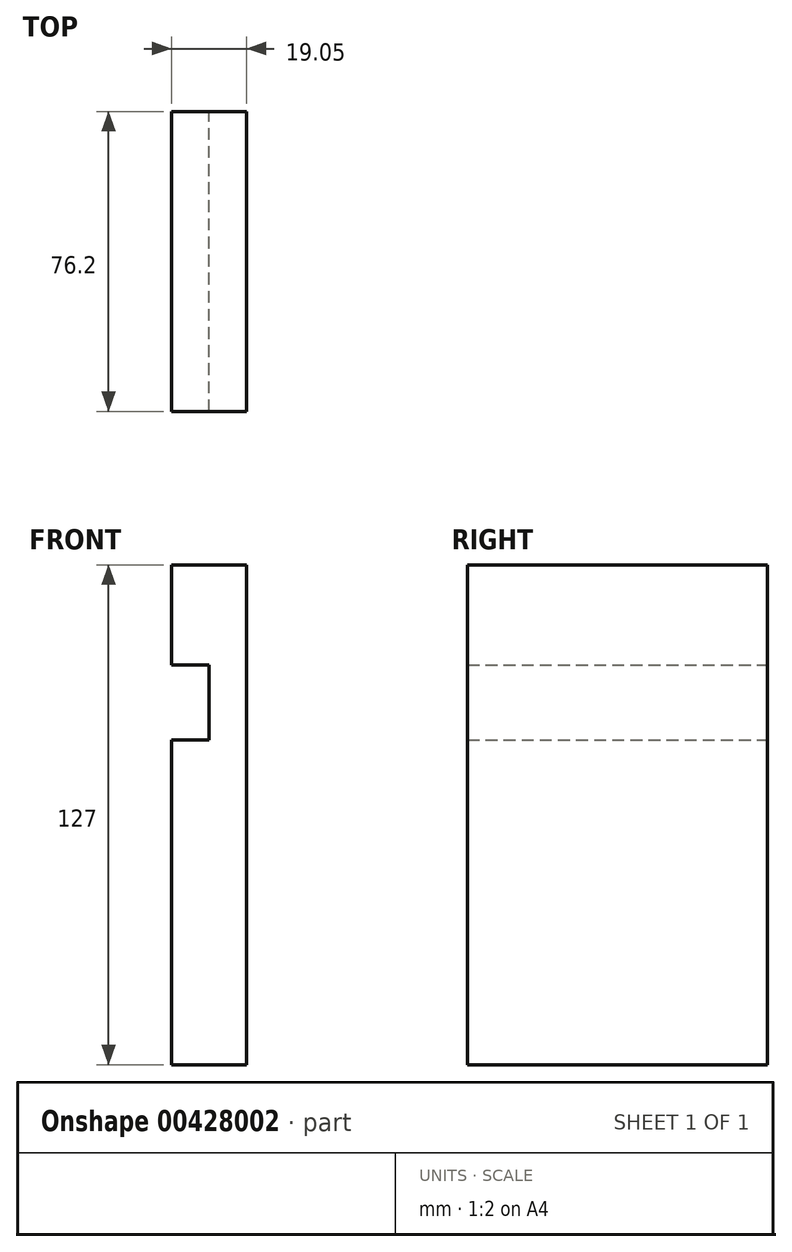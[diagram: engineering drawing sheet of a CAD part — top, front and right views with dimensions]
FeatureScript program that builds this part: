
annotation { "Feature Type Name" : "Feature", "Feature Type Description" : "" }
export const myFeature = defineFeature(function(context is Context, id is Id, definition is map)
    precondition{}
    {
        {
            var Q0;
            Q0=qCreatedBy(makeId("Front.planeOp"),FACE);
            var sketch = newSketch(context, id + "F0", { "sketchPlane" : qUnion([Q0])});
            skLineSegment(sketch, "E0", {"start": v(0, 0) * mm, "end": v(0, 127) * mm});
            skLineSegment(sketch, "E1", {"start": v(0, 0) * mm, "end": v(-19.05, 0) * mm});
            skLineSegment(sketch, "E2", {"start": v(0, 127) * mm, "end": v(-19.05, 127) * mm});
            skLineSegment(sketch, "E3", {"start": v(-19.05, 127) * mm, "end": v(-19.05, 101.6) * mm});
            skLineSegment(sketch, "E4", {"start": v(-19.05, 101.6) * mm, "end": v(-9.53, 101.6) * mm});
            skLineSegment(sketch, "E5", {"start": v(-9.53, 101.6) * mm, "end": v(-9.53, 82.55) * mm});
            skLineSegment(sketch, "E6", {"start": v(-9.53, 82.55) * mm, "end": v(-19.05, 82.55) * mm});
            skLineSegment(sketch, "E7", {"start": v(-19.05, 82.55) * mm, "end": v(-19.05, 0) * mm});
            skSolve(sketch);
        }
        {
            var Q0;
            Q0 = qSketchRegion(id + "F0", true);
            extrude(context, id + "F1", {"entities" : qUnion([Q0]), "depth" : 76.2 * mm});
        }
    });
